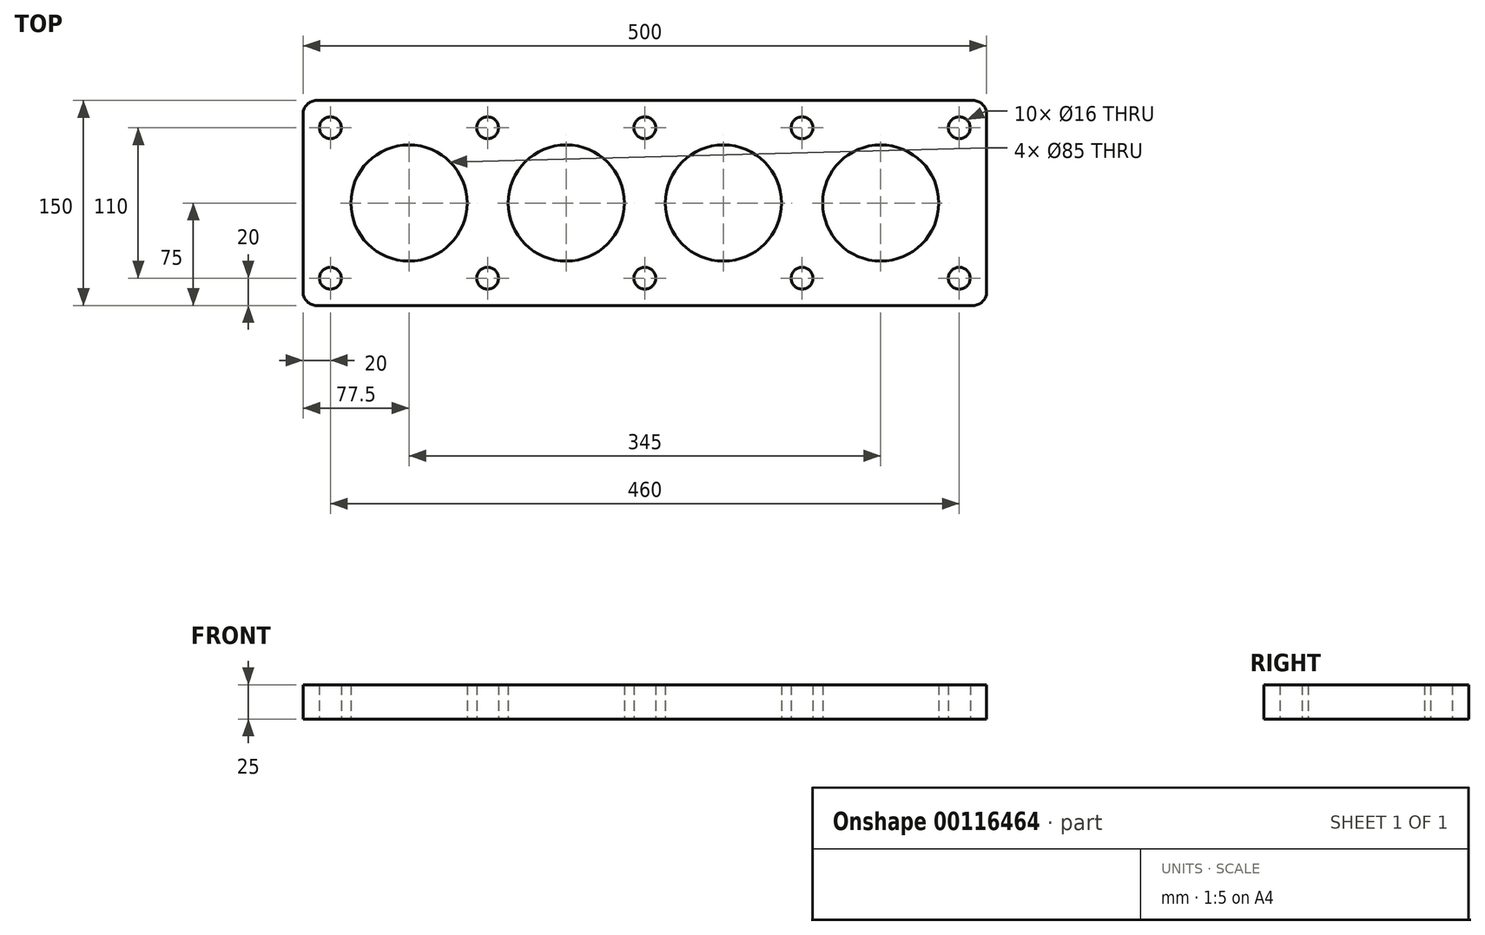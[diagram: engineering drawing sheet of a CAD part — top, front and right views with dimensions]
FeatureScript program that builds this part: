
annotation { "Feature Type Name" : "Feature", "Feature Type Description" : "" }
export const myFeature = defineFeature(function(context is Context, id is Id, definition is map)
    precondition{}
    {
        {
            var Q0;
            Q0=qCreatedBy(makeId("Top.planeOp"),FACE);
            var sketch = newSketch(context, id + "F2", { "sketchPlane" : qUnion([Q0])});
            skLineSegment(sketch, "E0", {"start": v(0, 0) * mm, "end": v(-240, 0) * mm});
            skLineSegment(sketch, "E1", {"start": v(-250, -10) * mm, "end": v(-250, -140) * mm});
            skLineSegment(sketch, "E2", {"start": v(-240, -150) * mm, "end": v(0, -150) * mm});
            skPoint(sketch, "E3.visualSharp", {"position": v(-250, 0) * mm});
            skArc(sketch, "E3.filletArc", {"start": v(-240, 0) * mm, "mid": v(-247.07, -2.93) * mm, "end": v(-250, -10) * mm});
            skPoint(sketch, "E4.visualSharp", {"position": v(-250, -150) * mm});
            skArc(sketch, "E4.filletArc", {"start": v(-250, -140) * mm, "mid": v(-247.07, -147.07) * mm, "end": v(-240, -150) * mm});
            skLineSegment(sketch, "E5", {"start": v(-276.86, -75) * mm, "end": v(-35.34, -75) * mm, "construction": true});
            skPoint(sketch, "E5.startSnap0", {"position": v(-250, -75) * mm});
            skCircle(sketch, "E6", {"center": v(-172.5, -75) * mm, "radius": 42.5 * mm});
            skCircle(sketch, "E7", {"center": v(-57.5, -75) * mm, "radius": 42.5 * mm});
            skLineSegment(sketch, "E8", {"start": v(-230, -130) * mm, "end": v(-13.7, -130) * mm, "construction": true});
            skCircle(sketch, "E9", {"center": v(-230, -130) * mm, "radius": 8 * mm});
            skCircle(sketch, "E10", {"center": v(-115, -130) * mm, "radius": 8 * mm});
            skArc(sketch, "E11", {"start": v(0, -122) * mm, "mid": v(-8, -130) * mm, "end": v(0, -138) * mm});
            skArc(sketch, "E12.MirrorC", {"start": v(0, -28) * mm, "mid": v(-8, -20) * mm, "end": v(0, -12) * mm});
            skCircle(sketch, "E13.MirrorC", {"center": v(-115, -20) * mm, "radius": 8 * mm});
            skCircle(sketch, "E14.MirrorC", {"center": v(-230, -20) * mm, "radius": 8 * mm});
            skLineSegment(sketch, "E15", {"start": v(0, 0) * mm, "end": v(0, -12) * mm});
            skLineSegment(sketch, "E16.trimOffspring", {"start": v(0, -138) * mm, "end": v(0, -150) * mm});
            skLineSegment(sketch, "E17.trimOffspring", {"start": v(0, -28) * mm, "end": v(0, -122) * mm});
            skSolve(sketch);
        }
        {
            var Q0;
            Q0=makeQuery(id+"F2.imprint","IMPRINT",FACE,{"disambiguationData":[TD([[makeQuery(id+"F2.imprint","IMPRINT",EDGE,{"derivedFrom":sQuery(id+"F2.wireOp",EDGE,"E0")}),1.0]])]});
            extrude(context, id + "F0", {"entities" : qUnion([Q0]), "depth" : 25 * mm});
        }
        {
            var Q0;
            Q0=makeQuery(id+"F0.opExtrude","SWEPT_BODY",BODY,{"disambiguationData":[OSD([sQuery(id+"F2.wireOp",EDGE,"E0"),sQuery(id+"F2.wireOp",EDGE,"E1"),sQuery(id+"F2.wireOp",EDGE,"E2"),sQuery(id+"F2.wireOp",EDGE,"E3.filletArc"),sQuery(id+"F2.wireOp",EDGE,"E4.filletArc"),sQuery(id+"F2.wireOp",EDGE,"E6"),sQuery(id+"F2.wireOp",EDGE,"E7"),sQuery(id+"F2.wireOp",EDGE,"E9"),sQuery(id+"F2.wireOp",EDGE,"E10"),sQuery(id+"F2.wireOp",EDGE,"E11"),sQuery(id+"F2.wireOp",EDGE,"E12.MirrorC"),sQuery(id+"F2.wireOp",EDGE,"E13.MirrorC"),sQuery(id+"F2.wireOp",EDGE,"E14.MirrorC"),sQuery(id+"F2.wireOp",EDGE,"E15"),sQuery(id+"F2.wireOp",EDGE,"E16.trimOffspring"),sQuery(id+"F2.wireOp",EDGE,"E17.trimOffspring")])]});
            var Q1;
            Q1=makeQuery(id+"F0.opExtrude","SWEPT_FACE",FACE,{"disambiguationData":[OSD([sQuery(id+"F2.wireOp",EDGE,"E17.trimOffspring")])]});
            mirror(context, id + "F1", {"operationType" : NewBodyOperationType.ADD, "entities" : qUnion([Q0]), "mirrorPlane" : qUnion([Q1])});
        }
    });
